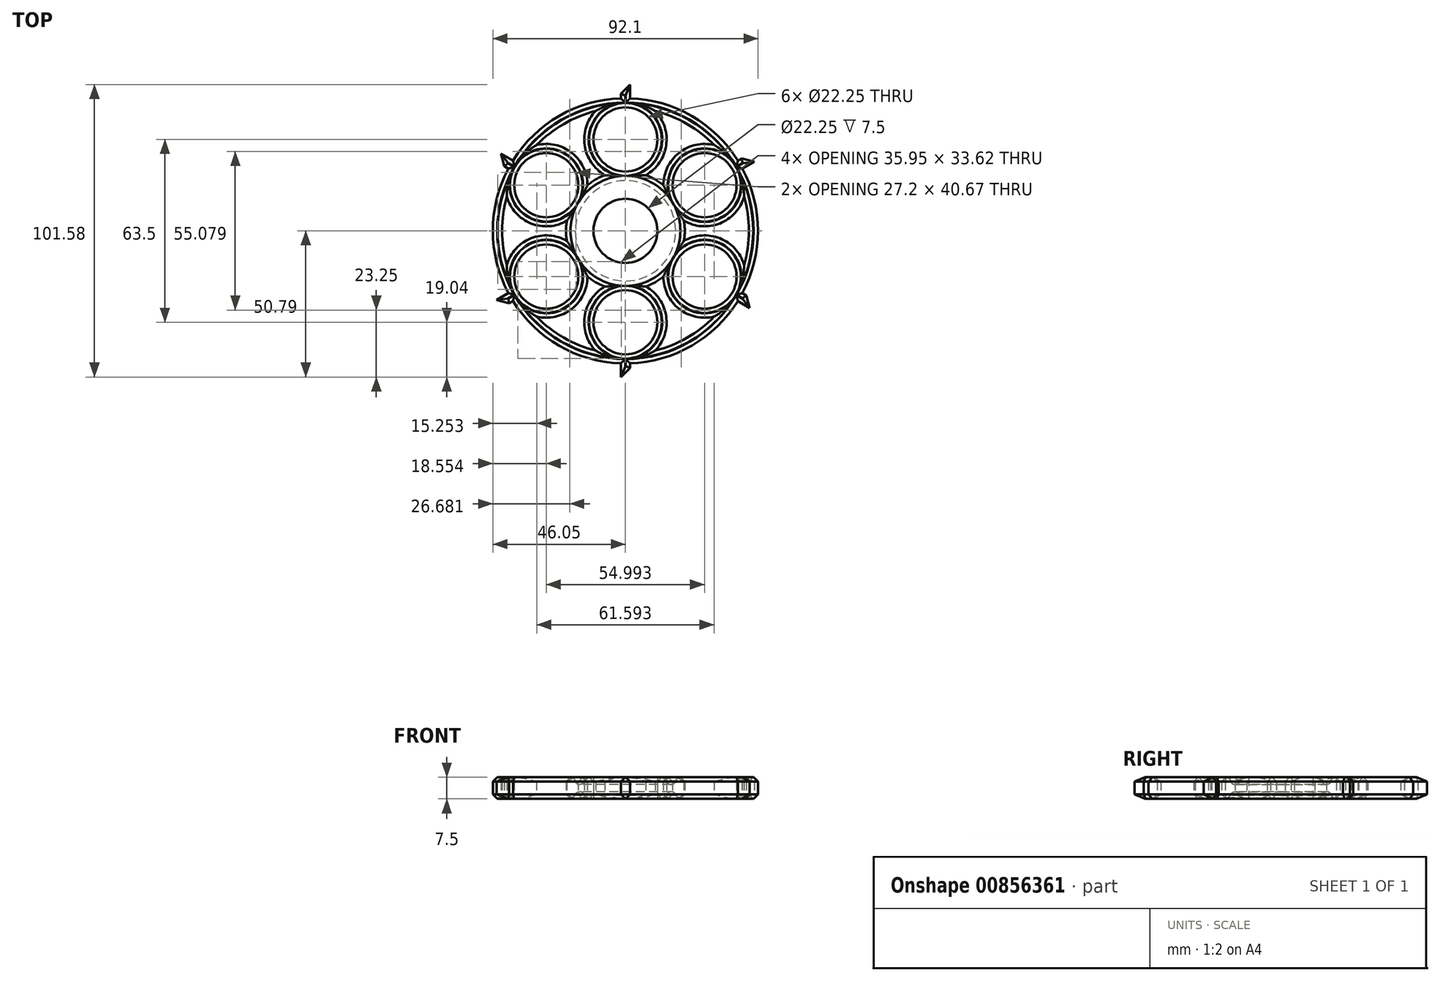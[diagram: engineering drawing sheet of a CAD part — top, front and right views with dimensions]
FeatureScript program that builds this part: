
annotation { "Feature Type Name" : "Feature", "Feature Type Description" : "" }
export const myFeature = defineFeature(function(context is Context, id is Id, definition is map)
    precondition{}
    {
        {
            var Q0;
            Q0=qCreatedBy(makeId("Top.planeOp"),FACE);
            var sketch = newSketch(context, id + "F0", { "sketchPlane" : qUnion([Q0])});
            skCircle(sketch, "E0", {"center": v(0, 0) * mm, "radius": 11.12 * mm});
            skCircle(sketch, "E1", {"center": v(0, 31.75) * mm, "radius": 11.12 * mm});
            skCircle(sketch, "E2", {"center": v(0, -31.75) * mm, "radius": 11.12 * mm});
            skCircle(sketch, "E3", {"center": v(0, 31.75) * mm, "radius": 14.3 * mm});
            skCircle(sketch, "E4", {"center": v(0, 0) * mm, "radius": 14.3 * mm});
            skCircle(sketch, "E5", {"center": v(0, -31.75) * mm, "radius": 14.3 * mm});
            skCircle(sketch, "E6", {"center": v(0, 0) * mm, "radius": 42.88 * mm});
            skCircle(sketch, "E7", {"center": v(0, 0) * mm, "radius": 46.05 * mm});
            skCircle(sketch, "E8.1.0", {"center": v(27.5, 15.87) * mm, "radius": 14.3 * mm});
            skCircle(sketch, "E8.1.1", {"center": v(27.5, 15.87) * mm, "radius": 11.12 * mm});
            skCircle(sketch, "E8.1.2", {"center": v(-27.5, -15.87) * mm, "radius": 11.12 * mm});
            skCircle(sketch, "E8.1.3", {"center": v(-27.5, -15.87) * mm, "radius": 14.3 * mm});
            skCircle(sketch, "E8.2.0", {"center": v(-27.5, 15.88) * mm, "radius": 14.3 * mm});
            skCircle(sketch, "E8.2.1", {"center": v(-27.5, 15.88) * mm, "radius": 11.12 * mm});
            skCircle(sketch, "E8.2.2", {"center": v(27.5, -15.88) * mm, "radius": 11.12 * mm});
            skCircle(sketch, "E8.2.3", {"center": v(27.5, -15.88) * mm, "radius": 14.3 * mm});
            skCircle(sketch, "E9", {"center": v(0, 0) * mm, "radius": 20.62 * mm});
            skCircle(sketch, "E10", {"center": v(0, 0) * mm, "radius": 17.45 * mm});
            skLineSegment(sketch, "E11.bottom", {"start": v(-1.59, 44.46) * mm, "end": v(1.59, 44.46) * mm});
            skLineSegment(sketch, "E11.top", {"start": v(-1.59, 50.79) * mm, "end": v(1.59, 50.79) * mm});
            skLineSegment(sketch, "E11.left", {"start": v(-1.59, 44.46) * mm, "end": v(-1.59, 50.79) * mm});
            skLineSegment(sketch, "E11.right", {"start": v(1.59, 44.46) * mm, "end": v(1.59, 50.79) * mm});
            skPoint(sketch, "E11.middle", {"position": v(0, 47.62) * mm});
            skCircle(sketch, "E12", {"center": v(0, 63.5) * mm, "radius": 11.12 * mm});
            skLineSegment(sketch, "E13", {"start": v(1.59, 50.79) * mm, "end": v(-1.59, 47.61) * mm});
            skLineSegment(sketch, "E14.1.0", {"start": v(-39.3, 20.86) * mm, "end": v(-37.71, 23.6) * mm});
            skLineSegment(sketch, "E14.1.1", {"start": v(-37.71, 23.6) * mm, "end": v(-43.19, 26.77) * mm});
            skLineSegment(sketch, "E14.1.2", {"start": v(-43.19, 26.77) * mm, "end": v(-42.03, 22.43) * mm});
            skLineSegment(sketch, "E14.1.3", {"start": v(-39.3, 20.86) * mm, "end": v(-44.78, 24.02) * mm});
            skLineSegment(sketch, "E14.2.0", {"start": v(-37.71, -23.6) * mm, "end": v(-39.3, -20.86) * mm});
            skLineSegment(sketch, "E14.2.1", {"start": v(-39.3, -20.86) * mm, "end": v(-44.78, -24.02) * mm});
            skLineSegment(sketch, "E14.2.2", {"start": v(-44.78, -24.02) * mm, "end": v(-40.44, -25.18) * mm});
            skLineSegment(sketch, "E14.2.3", {"start": v(-37.71, -23.6) * mm, "end": v(-43.19, -26.77) * mm});
            skLineSegment(sketch, "E14.3.0", {"start": v(1.59, -44.46) * mm, "end": v(-1.59, -44.46) * mm});
            skLineSegment(sketch, "E14.3.1", {"start": v(-1.59, -44.46) * mm, "end": v(-1.59, -50.79) * mm});
            skLineSegment(sketch, "E14.3.2", {"start": v(-1.59, -50.79) * mm, "end": v(1.59, -47.61) * mm});
            skLineSegment(sketch, "E14.3.3", {"start": v(1.59, -44.46) * mm, "end": v(1.59, -50.79) * mm});
            skLineSegment(sketch, "E14.4.0", {"start": v(39.3, -20.86) * mm, "end": v(37.71, -23.6) * mm});
            skLineSegment(sketch, "E14.4.1", {"start": v(37.71, -23.6) * mm, "end": v(43.19, -26.77) * mm});
            skLineSegment(sketch, "E14.4.2", {"start": v(43.19, -26.77) * mm, "end": v(42.03, -22.43) * mm});
            skLineSegment(sketch, "E14.4.3", {"start": v(39.3, -20.86) * mm, "end": v(44.78, -24.02) * mm});
            skLineSegment(sketch, "E14.5.0", {"start": v(37.71, 23.6) * mm, "end": v(39.3, 20.86) * mm});
            skLineSegment(sketch, "E14.5.1", {"start": v(39.3, 20.86) * mm, "end": v(44.78, 24.02) * mm});
            skLineSegment(sketch, "E14.5.2", {"start": v(44.78, 24.02) * mm, "end": v(40.44, 25.18) * mm});
            skLineSegment(sketch, "E14.5.3", {"start": v(37.71, 23.6) * mm, "end": v(43.19, 26.77) * mm});
            skSolve(sketch);
        }
        {
            var Q0;
            {var subQ0=sQuery(id+"F0.wireOp",EDGE,"E6");var subQ1=sQuery(id+"F0.wireOp",EDGE,"E1");var subQ2=makeQuery(id+"F0.imprint","INTERSECT",VERTEX,{"derivedFrom":[subQ1,subQ0]});Q0=makeQuery(id+"F0.imprint","IMPRINT",FACE,{"disambiguationData":[TD([[makeQuery(id+"F0.imprint","IMPRINT",EDGE,{"disambiguationData":[TD([[subQ2,1.0]])],"derivedFrom":subQ1}),-1.0]])]});}
            var Q1;
            {var subQ0=sQuery(id+"F0.wireOp",EDGE,"E6");var subQ1=sQuery(id+"F0.wireOp",EDGE,"E1");var subQ2=makeQuery(id+"F0.imprint","INTERSECT",VERTEX,{"derivedFrom":[subQ1,subQ0]});Q1=makeQuery(id+"F0.imprint","IMPRINT",FACE,{"disambiguationData":[TD([[makeQuery(id+"F0.imprint","IMPRINT",EDGE,{"disambiguationData":[TD([[subQ2,-1.0]])],"derivedFrom":subQ1}),-1.0]])]});}
            var Q2;
            {var subQ0=sQuery(id+"F0.wireOp",EDGE,"E9");var subQ1=sQuery(id+"F0.wireOp",EDGE,"E3");var subQ2=makeQuery(id+"F0.imprint","INTERSECT",VERTEX,{"disambiguationData":[OD(0.0)],"derivedFrom":[subQ1,subQ0]});Q2=makeQuery(id+"F0.imprint","IMPRINT",FACE,{"disambiguationData":[TD([[makeQuery(id+"F0.imprint","IMPRINT",EDGE,{"disambiguationData":[TD([[subQ2,-1.0]])],"derivedFrom":subQ1}),1.0]])]});}
            var Q3;
            {var subQ0=sQuery(id+"F0.wireOp",EDGE,"E8.1.0");var subQ1=makeQuery(id+"F0.imprint","INTERSECT",VERTEX,{"derivedFrom":[subQ0,sQuery(id+"F0.wireOp",EDGE,"E10")]});Q3=makeQuery(id+"F0.imprint","IMPRINT",FACE,{"disambiguationData":[TD([[makeQuery(id+"F0.imprint","IMPRINT",EDGE,{"disambiguationData":[TD([[subQ1,1.0]])],"derivedFrom":subQ0}),1.0]])]});}
            var Q4;
            {var subQ0=sQuery(id+"F0.wireOp",EDGE,"E10");var subQ1=sQuery(id+"F0.wireOp",EDGE,"E3");var subQ2=makeQuery(id+"F0.imprint","INTERSECT",VERTEX,{"derivedFrom":[subQ1,subQ0]});Q4=makeQuery(id+"F0.imprint","IMPRINT",FACE,{"disambiguationData":[TD([[makeQuery(id+"F0.imprint","IMPRINT",EDGE,{"disambiguationData":[TD([[subQ2,-1.0]])],"derivedFrom":subQ1}),-1.0]])]});}
            var Q5;
            {var subQ0=sQuery(id+"F0.wireOp",EDGE,"E10");var subQ1=sQuery(id+"F0.wireOp",EDGE,"E8.1.0");var subQ2=makeQuery(id+"F0.imprint","INTERSECT",VERTEX,{"derivedFrom":[subQ1,subQ0]});Q5=makeQuery(id+"F0.imprint","IMPRINT",FACE,{"disambiguationData":[TD([[makeQuery(id+"F0.imprint","IMPRINT",EDGE,{"disambiguationData":[TD([[subQ2,-1.0]])],"derivedFrom":subQ1}),-1.0]])]});}
            var Q6;
            {var subQ0=sQuery(id+"F0.wireOp",EDGE,"E9");var subQ1=sQuery(id+"F0.wireOp",EDGE,"E8.2.3");var subQ2=makeQuery(id+"F0.imprint","INTERSECT",VERTEX,{"disambiguationData":[OD(0.0)],"derivedFrom":[subQ1,subQ0]});Q6=makeQuery(id+"F0.imprint","IMPRINT",FACE,{"disambiguationData":[TD([[makeQuery(id+"F0.imprint","IMPRINT",EDGE,{"disambiguationData":[TD([[subQ2,-1.0]])],"derivedFrom":subQ1}),1.0]])]});}
            var Q7;
            {var subQ0=sQuery(id+"F0.wireOp",EDGE,"E10");var subQ1=sQuery(id+"F0.wireOp",EDGE,"E5");var subQ2=makeQuery(id+"F0.imprint","INTERSECT",VERTEX,{"derivedFrom":[subQ1,subQ0]});Q7=makeQuery(id+"F0.imprint","IMPRINT",FACE,{"disambiguationData":[TD([[makeQuery(id+"F0.imprint","IMPRINT",EDGE,{"disambiguationData":[TD([[subQ2,1.0]])],"derivedFrom":subQ1}),-1.0]])]});}
            var Q8;
            {var subQ0=sQuery(id+"F0.wireOp",EDGE,"E5");var subQ1=makeQuery(id+"F0.imprint","INTERSECT",VERTEX,{"derivedFrom":[subQ0,sQuery(id+"F0.wireOp",EDGE,"E10")]});Q8=makeQuery(id+"F0.imprint","IMPRINT",FACE,{"disambiguationData":[TD([[makeQuery(id+"F0.imprint","IMPRINT",EDGE,{"disambiguationData":[TD([[subQ1,1.0]])],"derivedFrom":subQ0}),1.0]])]});}
            var Q9;
            {var subQ0=sQuery(id+"F0.wireOp",EDGE,"E10");var subQ1=sQuery(id+"F0.wireOp",EDGE,"E5");var subQ2=makeQuery(id+"F0.imprint","INTERSECT",VERTEX,{"derivedFrom":[subQ1,subQ0]});Q9=makeQuery(id+"F0.imprint","IMPRINT",FACE,{"disambiguationData":[TD([[makeQuery(id+"F0.imprint","IMPRINT",EDGE,{"disambiguationData":[TD([[subQ2,-1.0]])],"derivedFrom":subQ1}),-1.0]])]});}
            var Q10;
            {var subQ0=sQuery(id+"F0.wireOp",EDGE,"E9");var subQ1=sQuery(id+"F0.wireOp",EDGE,"E8.1.3");var subQ2=makeQuery(id+"F0.imprint","INTERSECT",VERTEX,{"disambiguationData":[OD(0.0)],"derivedFrom":[subQ1,subQ0]});Q10=makeQuery(id+"F0.imprint","IMPRINT",FACE,{"disambiguationData":[TD([[makeQuery(id+"F0.imprint","IMPRINT",EDGE,{"disambiguationData":[TD([[subQ2,-1.0]])],"derivedFrom":subQ1}),1.0]])]});}
            var Q11;
            {var subQ0=sQuery(id+"F0.wireOp",EDGE,"E10");var subQ1=sQuery(id+"F0.wireOp",EDGE,"E8.1.3");var subQ2=makeQuery(id+"F0.imprint","INTERSECT",VERTEX,{"derivedFrom":[subQ1,subQ0]});Q11=makeQuery(id+"F0.imprint","IMPRINT",FACE,{"disambiguationData":[TD([[makeQuery(id+"F0.imprint","IMPRINT",EDGE,{"disambiguationData":[TD([[subQ2,-1.0]])],"derivedFrom":subQ1}),-1.0]])]});}
            var Q12;
            {var subQ0=sQuery(id+"F0.wireOp",EDGE,"E8.2.0");var subQ1=makeQuery(id+"F0.imprint","INTERSECT",VERTEX,{"derivedFrom":[subQ0,sQuery(id+"F0.wireOp",EDGE,"E10")]});Q12=makeQuery(id+"F0.imprint","IMPRINT",FACE,{"disambiguationData":[TD([[makeQuery(id+"F0.imprint","IMPRINT",EDGE,{"disambiguationData":[TD([[subQ1,1.0]])],"derivedFrom":subQ0}),1.0]])]});}
            var Q13;
            {var subQ0=sQuery(id+"F0.wireOp",EDGE,"E9");var subQ1=sQuery(id+"F0.wireOp",EDGE,"E3");var subQ2=makeQuery(id+"F0.imprint","INTERSECT",VERTEX,{"disambiguationData":[OD(0.0)],"derivedFrom":[subQ1,subQ0]});Q13=makeQuery(id+"F0.imprint","IMPRINT",FACE,{"disambiguationData":[TD([[makeQuery(id+"F0.imprint","IMPRINT",EDGE,{"disambiguationData":[TD([[subQ2,-1.0]])],"derivedFrom":subQ1}),-1.0]])]});}
            var Q14;
            {var subQ0=sQuery(id+"F0.wireOp",EDGE,"E8.2.0");var subQ1=sQuery(id+"F0.wireOp",EDGE,"E6");var subQ2=makeQuery(id+"F0.imprint","INTERSECT",VERTEX,{"disambiguationData":[OD(0.0)],"derivedFrom":[subQ1,subQ0]});Q14=makeQuery(id+"F0.imprint","IMPRINT",FACE,{"disambiguationData":[TD([[makeQuery(id+"F0.imprint","IMPRINT",EDGE,{"disambiguationData":[TD([[subQ2,-1.0]])],"derivedFrom":subQ1}),1.0]])]});}
            var Q15;
            {var subQ0=sQuery(id+"F0.wireOp",EDGE,"E8.2.1");var subQ1=sQuery(id+"F0.wireOp",EDGE,"E6");var subQ2=makeQuery(id+"F0.imprint","INTERSECT",VERTEX,{"derivedFrom":[subQ1,subQ0]});Q15=makeQuery(id+"F0.imprint","IMPRINT",FACE,{"disambiguationData":[TD([[makeQuery(id+"F0.imprint","IMPRINT",EDGE,{"disambiguationData":[TD([[subQ2,-1.0]])],"derivedFrom":subQ1}),1.0]])]});}
            var Q16;
            {var subQ0=sQuery(id+"F0.wireOp",EDGE,"E8.1.1");var subQ1=sQuery(id+"F0.wireOp",EDGE,"E6");var subQ2=makeQuery(id+"F0.imprint","INTERSECT",VERTEX,{"derivedFrom":[subQ1,subQ0]});Q16=makeQuery(id+"F0.imprint","IMPRINT",FACE,{"disambiguationData":[TD([[makeQuery(id+"F0.imprint","IMPRINT",EDGE,{"disambiguationData":[TD([[subQ2,-1.0]])],"derivedFrom":subQ1}),1.0]])]});}
            var Q17;
            {var subQ0=sQuery(id+"F0.wireOp",EDGE,"E8.1.1");var subQ1=sQuery(id+"F0.wireOp",EDGE,"E6");var subQ2=makeQuery(id+"F0.imprint","INTERSECT",VERTEX,{"derivedFrom":[subQ1,subQ0]});Q17=makeQuery(id+"F0.imprint","IMPRINT",FACE,{"disambiguationData":[TD([[makeQuery(id+"F0.imprint","IMPRINT",EDGE,{"disambiguationData":[TD([[subQ2,1.0]])],"derivedFrom":subQ1}),1.0]])]});}
            var Q18;
            {var subQ0=sQuery(id+"F0.wireOp",EDGE,"E8.2.2");var subQ1=sQuery(id+"F0.wireOp",EDGE,"E6");var subQ2=makeQuery(id+"F0.imprint","INTERSECT",VERTEX,{"derivedFrom":[subQ1,subQ0]});Q18=makeQuery(id+"F0.imprint","IMPRINT",FACE,{"disambiguationData":[TD([[makeQuery(id+"F0.imprint","IMPRINT",EDGE,{"disambiguationData":[TD([[subQ2,-1.0]])],"derivedFrom":subQ1}),1.0]])]});}
            var Q19;
            {var subQ0=sQuery(id+"F0.wireOp",EDGE,"E8.2.3");var subQ1=sQuery(id+"F0.wireOp",EDGE,"E6");var subQ2=makeQuery(id+"F0.imprint","INTERSECT",VERTEX,{"disambiguationData":[OD(0.0)],"derivedFrom":[subQ1,subQ0]});Q19=makeQuery(id+"F0.imprint","IMPRINT",FACE,{"disambiguationData":[TD([[makeQuery(id+"F0.imprint","IMPRINT",EDGE,{"disambiguationData":[TD([[subQ2,-1.0]])],"derivedFrom":subQ1}),1.0]])]});}
            var Q20;
            {var subQ0=sQuery(id+"F0.wireOp",EDGE,"E6");var subQ1=sQuery(id+"F0.wireOp",EDGE,"E2");var subQ2=makeQuery(id+"F0.imprint","INTERSECT",VERTEX,{"derivedFrom":[subQ1,subQ0]});Q20=makeQuery(id+"F0.imprint","IMPRINT",FACE,{"disambiguationData":[TD([[makeQuery(id+"F0.imprint","IMPRINT",EDGE,{"disambiguationData":[TD([[subQ2,1.0]])],"derivedFrom":subQ1}),-1.0]])]});}
            var Q21;
            {var subQ0=sQuery(id+"F0.wireOp",EDGE,"E6");var subQ1=sQuery(id+"F0.wireOp",EDGE,"E2");var subQ2=makeQuery(id+"F0.imprint","INTERSECT",VERTEX,{"derivedFrom":[subQ1,subQ0]});Q21=makeQuery(id+"F0.imprint","IMPRINT",FACE,{"disambiguationData":[TD([[makeQuery(id+"F0.imprint","IMPRINT",EDGE,{"disambiguationData":[TD([[subQ2,-1.0]])],"derivedFrom":subQ1}),-1.0]])]});}
            var Q22;
            {var subQ0=sQuery(id+"F0.wireOp",EDGE,"E8.1.2");var subQ1=sQuery(id+"F0.wireOp",EDGE,"E6");var subQ2=makeQuery(id+"F0.imprint","INTERSECT",VERTEX,{"derivedFrom":[subQ1,subQ0]});Q22=makeQuery(id+"F0.imprint","IMPRINT",FACE,{"disambiguationData":[TD([[makeQuery(id+"F0.imprint","IMPRINT",EDGE,{"disambiguationData":[TD([[subQ2,-1.0]])],"derivedFrom":subQ1}),1.0]])]});}
            var Q23;
            {var subQ0=sQuery(id+"F0.wireOp",EDGE,"E8.1.3");var subQ1=sQuery(id+"F0.wireOp",EDGE,"E6");var subQ2=makeQuery(id+"F0.imprint","INTERSECT",VERTEX,{"disambiguationData":[OD(0.0)],"derivedFrom":[subQ1,subQ0]});Q23=makeQuery(id+"F0.imprint","IMPRINT",FACE,{"disambiguationData":[TD([[makeQuery(id+"F0.imprint","IMPRINT",EDGE,{"disambiguationData":[TD([[subQ2,-1.0]])],"derivedFrom":subQ1}),1.0]])]});}
            var Q24;
            Q24=makeQuery(id+"F0.imprint","IMPRINT",FACE,{"disambiguationData":[TD([[makeQuery(id+"F0.imprint","IMPRINT",EDGE,{"derivedFrom":sQuery(id+"F0.wireOp",EDGE,"E0")}),-1.0]])]});
            var Q25;
            Q25=makeQuery(id+"F0.imprint","IMPRINT",FACE,{"disambiguationData":[TD([[makeQuery(id+"F0.imprint","IMPRINT",EDGE,{"derivedFrom":sQuery(id+"F0.wireOp",EDGE,"E4")}),-1.0]])]});
            var Q26;
            {var subQ5=sQuery(id+"F0.wireOp",EDGE,"E11.left");var subQ8=sQuery(id+"F0.wireOp",EDGE,"E3");var subQ9=makeQuery(id+"F0.imprint","INTERSECT",VERTEX,{"derivedFrom":[subQ8,subQ5]});Q26=makeQuery(id+"F0.imprint","IMPRINT",FACE,{"disambiguationData":[TD([[makeQuery(id+"F0.imprint","IMPRINT",EDGE,{"disambiguationData":[TD([[subQ9,-1.0]])],"derivedFrom":subQ8}),-1.0]])]});}
            var Q27;
            {var subQ9=sQuery(id+"F0.wireOp",EDGE,"E14.1.0");Q27=makeQuery(id+"F0.imprint","IMPRINT",FACE,{"disambiguationData":[TD([[makeQuery(id+"F0.imprint","IMPRINT",EDGE,{"derivedFrom":subQ9}),-1.0]])]});}
            var Q28;
            {var subQ7=sQuery(id+"F0.wireOp",EDGE,"E11.bottom");Q28=makeQuery(id+"F0.imprint","IMPRINT",FACE,{"disambiguationData":[TD([[makeQuery(id+"F0.imprint","IMPRINT",EDGE,{"derivedFrom":subQ7}),-1.0]])]});}
            var Q29;
            {var subQ3=sQuery(id+"F0.wireOp",EDGE,"E11.right");var subQ9=sQuery(id+"F0.wireOp",EDGE,"E3");var subQ11=makeQuery(id+"F0.imprint","INTERSECT",VERTEX,{"derivedFrom":[subQ9,subQ3]});Q29=makeQuery(id+"F0.imprint","IMPRINT",FACE,{"disambiguationData":[TD([[makeQuery(id+"F0.imprint","IMPRINT",EDGE,{"disambiguationData":[TD([[subQ11,1.0]])],"derivedFrom":subQ9}),-1.0]])]});}
            var Q30;
            {var subQ0=sQuery(id+"F0.wireOp",EDGE,"E8.2.0");var subQ1=sQuery(id+"F0.wireOp",EDGE,"E6");var subQ2=makeQuery(id+"F0.imprint","INTERSECT",VERTEX,{"disambiguationData":[OD(1.0)],"derivedFrom":[subQ1,subQ0]});Q30=makeQuery(id+"F0.imprint","IMPRINT",FACE,{"disambiguationData":[TD([[makeQuery(id+"F0.imprint","IMPRINT",EDGE,{"disambiguationData":[TD([[subQ2,-1.0]])],"derivedFrom":subQ1}),-1.0]])]});}
            var Q31;
            {var subQ9=sQuery(id+"F0.wireOp",EDGE,"E14.5.0");Q31=makeQuery(id+"F0.imprint","IMPRINT",FACE,{"disambiguationData":[TD([[makeQuery(id+"F0.imprint","IMPRINT",EDGE,{"derivedFrom":subQ9}),-1.0]])]});}
            var Q32;
            {var subQ1=sQuery(id+"F0.wireOp",EDGE,"E6");var subQ5=sQuery(id+"F0.wireOp",EDGE,"E8.1.0");var subQ6=makeQuery(id+"F0.imprint","INTERSECT",VERTEX,{"disambiguationData":[OD(0.0)],"derivedFrom":[subQ1,subQ5]});Q32=makeQuery(id+"F0.imprint","IMPRINT",FACE,{"disambiguationData":[TD([[makeQuery(id+"F0.imprint","IMPRINT",EDGE,{"disambiguationData":[TD([[subQ6,1.0]])],"derivedFrom":subQ1}),-1.0]])]});}
            var Q33;
            {var subQ9=sQuery(id+"F0.wireOp",EDGE,"E14.4.0");Q33=makeQuery(id+"F0.imprint","IMPRINT",FACE,{"disambiguationData":[TD([[makeQuery(id+"F0.imprint","IMPRINT",EDGE,{"derivedFrom":subQ9}),-1.0]])]});}
            var Q34;
            {var subQ0=sQuery(id+"F0.wireOp",EDGE,"E14.3.3");var subQ6=sQuery(id+"F0.wireOp",EDGE,"E5");var subQ11=makeQuery(id+"F0.imprint","INTERSECT",VERTEX,{"derivedFrom":[subQ6,subQ0]});Q34=makeQuery(id+"F0.imprint","IMPRINT",FACE,{"disambiguationData":[TD([[makeQuery(id+"F0.imprint","IMPRINT",EDGE,{"disambiguationData":[TD([[subQ11,-1.0]])],"derivedFrom":subQ6}),-1.0]])]});}
            var Q35;
            {var subQ9=sQuery(id+"F0.wireOp",EDGE,"E14.3.0");Q35=makeQuery(id+"F0.imprint","IMPRINT",FACE,{"disambiguationData":[TD([[makeQuery(id+"F0.imprint","IMPRINT",EDGE,{"derivedFrom":subQ9}),-1.0]])]});}
            var Q36;
            {var subQ6=sQuery(id+"F0.wireOp",EDGE,"E6");var subQ9=sQuery(id+"F0.wireOp",EDGE,"E5");var subQ10=makeQuery(id+"F0.imprint","INTERSECT",VERTEX,{"disambiguationData":[OD(0.0)],"derivedFrom":[subQ9,subQ6]});Q36=makeQuery(id+"F0.imprint","IMPRINT",FACE,{"disambiguationData":[TD([[makeQuery(id+"F0.imprint","IMPRINT",EDGE,{"disambiguationData":[TD([[subQ10,-1.0]])],"derivedFrom":subQ9}),-1.0]])]});}
            var Q37;
            {var subQ9=sQuery(id+"F0.wireOp",EDGE,"E14.2.0");Q37=makeQuery(id+"F0.imprint","IMPRINT",FACE,{"disambiguationData":[TD([[makeQuery(id+"F0.imprint","IMPRINT",EDGE,{"derivedFrom":subQ9}),-1.0]])]});}
            var Q38;
            {var subQ1=sQuery(id+"F0.wireOp",EDGE,"E11.bottom");Q38=makeQuery(id+"F0.imprint","IMPRINT",FACE,{"disambiguationData":[TD([[makeQuery(id+"F0.imprint","IMPRINT",EDGE,{"derivedFrom":subQ1}),1.0]])]});}
            var Q39;
            {var subQ0=sQuery(id+"F0.wireOp",EDGE,"E13");Q39=makeQuery(id+"F0.imprint","IMPRINT",FACE,{"disambiguationData":[TD([[makeQuery(id+"F0.imprint","IMPRINT",EDGE,{"derivedFrom":subQ0}),1.0]])]});}
            var Q40;
            {var subQ0=sQuery(id+"F0.wireOp",EDGE,"E11.right");var subQ1=sQuery(id+"F0.wireOp",EDGE,"E3");var subQ2=makeQuery(id+"F0.imprint","INTERSECT",VERTEX,{"derivedFrom":[subQ1,subQ0]});Q40=makeQuery(id+"F0.imprint","IMPRINT",FACE,{"disambiguationData":[TD([[makeQuery(id+"F0.imprint","IMPRINT",EDGE,{"disambiguationData":[TD([[subQ2,-1.0]])],"derivedFrom":subQ1}),-1.0]])]});}
            var Q41;
            {var subQ0=sQuery(id+"F0.wireOp",EDGE,"E7");var subQ1=sQuery(id+"F0.wireOp",EDGE,"E3");var subQ2=makeQuery(id+"F0.imprint","INTERSECT",VERTEX,{"derivedFrom":[subQ1,subQ0]});Q41=makeQuery(id+"F0.imprint","IMPRINT",FACE,{"disambiguationData":[TD([[makeQuery(id+"F0.imprint","IMPRINT",EDGE,{"disambiguationData":[TD([[subQ2,-1.0]])],"derivedFrom":subQ1}),-1.0]])]});}
            var Q42;
            {var subQ0=sQuery(id+"F0.wireOp",EDGE,"E14.1.1");var subQ1=sQuery(id+"F0.wireOp",EDGE,"E7");var subQ2=makeQuery(id+"F0.imprint","INTERSECT",VERTEX,{"derivedFrom":[subQ1,subQ0]});Q42=makeQuery(id+"F0.imprint","IMPRINT",FACE,{"disambiguationData":[TD([[makeQuery(id+"F0.imprint","IMPRINT",EDGE,{"disambiguationData":[TD([[subQ2,-1.0]])],"derivedFrom":subQ1}),1.0]])]});}
            var Q43;
            {var subQ1=sQuery(id+"F0.wireOp",EDGE,"E14.1.0");Q43=makeQuery(id+"F0.imprint","IMPRINT",FACE,{"disambiguationData":[TD([[makeQuery(id+"F0.imprint","IMPRINT",EDGE,{"derivedFrom":subQ1}),1.0]])]});}
            var Q44;
            {var subQ0=sQuery(id+"F0.wireOp",EDGE,"E14.1.2");Q44=makeQuery(id+"F0.imprint","IMPRINT",FACE,{"disambiguationData":[TD([[makeQuery(id+"F0.imprint","IMPRINT",EDGE,{"derivedFrom":subQ0}),1.0]])]});}
            var Q45;
            {var subQ0=sQuery(id+"F0.wireOp",EDGE,"E14.1.3");var subQ1=sQuery(id+"F0.wireOp",EDGE,"E7");var subQ2=makeQuery(id+"F0.imprint","INTERSECT",VERTEX,{"derivedFrom":[subQ1,subQ0]});Q45=makeQuery(id+"F0.imprint","IMPRINT",FACE,{"disambiguationData":[TD([[makeQuery(id+"F0.imprint","IMPRINT",EDGE,{"disambiguationData":[TD([[subQ2,1.0]])],"derivedFrom":subQ1}),1.0]])]});}
            var Q46;
            {var subQ0=sQuery(id+"F0.wireOp",EDGE,"E14.2.1");var subQ1=sQuery(id+"F0.wireOp",EDGE,"E7");var subQ2=makeQuery(id+"F0.imprint","INTERSECT",VERTEX,{"derivedFrom":[subQ1,subQ0]});Q46=makeQuery(id+"F0.imprint","IMPRINT",FACE,{"disambiguationData":[TD([[makeQuery(id+"F0.imprint","IMPRINT",EDGE,{"disambiguationData":[TD([[subQ2,-1.0]])],"derivedFrom":subQ1}),1.0]])]});}
            var Q47;
            {var subQ1=sQuery(id+"F0.wireOp",EDGE,"E14.2.0");Q47=makeQuery(id+"F0.imprint","IMPRINT",FACE,{"disambiguationData":[TD([[makeQuery(id+"F0.imprint","IMPRINT",EDGE,{"derivedFrom":subQ1}),1.0]])]});}
            var Q48;
            {var subQ0=sQuery(id+"F0.wireOp",EDGE,"E14.2.3");var subQ1=sQuery(id+"F0.wireOp",EDGE,"E7");var subQ2=makeQuery(id+"F0.imprint","INTERSECT",VERTEX,{"derivedFrom":[subQ1,subQ0]});Q48=makeQuery(id+"F0.imprint","IMPRINT",FACE,{"disambiguationData":[TD([[makeQuery(id+"F0.imprint","IMPRINT",EDGE,{"disambiguationData":[TD([[subQ2,1.0]])],"derivedFrom":subQ1}),1.0]])]});}
            var Q49;
            {var subQ0=sQuery(id+"F0.wireOp",EDGE,"E14.2.2");Q49=makeQuery(id+"F0.imprint","IMPRINT",FACE,{"disambiguationData":[TD([[makeQuery(id+"F0.imprint","IMPRINT",EDGE,{"derivedFrom":subQ0}),1.0]])]});}
            var Q50;
            {var subQ1=sQuery(id+"F0.wireOp",EDGE,"E14.3.0");Q50=makeQuery(id+"F0.imprint","IMPRINT",FACE,{"disambiguationData":[TD([[makeQuery(id+"F0.imprint","IMPRINT",EDGE,{"derivedFrom":subQ1}),1.0]])]});}
            var Q51;
            {var subQ0=sQuery(id+"F0.wireOp",EDGE,"E14.3.1");var subQ1=sQuery(id+"F0.wireOp",EDGE,"E5");var subQ2=makeQuery(id+"F0.imprint","INTERSECT",VERTEX,{"derivedFrom":[subQ1,subQ0]});Q51=makeQuery(id+"F0.imprint","IMPRINT",FACE,{"disambiguationData":[TD([[makeQuery(id+"F0.imprint","IMPRINT",EDGE,{"disambiguationData":[TD([[subQ2,-1.0]])],"derivedFrom":subQ1}),-1.0]])]});}
            var Q52;
            {var subQ0=sQuery(id+"F0.wireOp",EDGE,"E14.3.2");Q52=makeQuery(id+"F0.imprint","IMPRINT",FACE,{"disambiguationData":[TD([[makeQuery(id+"F0.imprint","IMPRINT",EDGE,{"derivedFrom":subQ0}),1.0]])]});}
            var Q53;
            {var subQ0=sQuery(id+"F0.wireOp",EDGE,"E7");var subQ1=sQuery(id+"F0.wireOp",EDGE,"E5");var subQ2=makeQuery(id+"F0.imprint","INTERSECT",VERTEX,{"derivedFrom":[subQ1,subQ0]});Q53=makeQuery(id+"F0.imprint","IMPRINT",FACE,{"disambiguationData":[TD([[makeQuery(id+"F0.imprint","IMPRINT",EDGE,{"disambiguationData":[TD([[subQ2,-1.0]])],"derivedFrom":subQ1}),-1.0]])]});}
            var Q54;
            {var subQ1=sQuery(id+"F0.wireOp",EDGE,"E14.4.0");Q54=makeQuery(id+"F0.imprint","IMPRINT",FACE,{"disambiguationData":[TD([[makeQuery(id+"F0.imprint","IMPRINT",EDGE,{"derivedFrom":subQ1}),1.0]])]});}
            var Q55;
            {var subQ0=sQuery(id+"F0.wireOp",EDGE,"E14.4.3");var subQ1=sQuery(id+"F0.wireOp",EDGE,"E7");var subQ2=makeQuery(id+"F0.imprint","INTERSECT",VERTEX,{"derivedFrom":[subQ1,subQ0]});Q55=makeQuery(id+"F0.imprint","IMPRINT",FACE,{"disambiguationData":[TD([[makeQuery(id+"F0.imprint","IMPRINT",EDGE,{"disambiguationData":[TD([[subQ2,1.0]])],"derivedFrom":subQ1}),1.0]])]});}
            var Q56;
            {var subQ0=sQuery(id+"F0.wireOp",EDGE,"E14.4.2");Q56=makeQuery(id+"F0.imprint","IMPRINT",FACE,{"disambiguationData":[TD([[makeQuery(id+"F0.imprint","IMPRINT",EDGE,{"derivedFrom":subQ0}),1.0]])]});}
            var Q57;
            {var subQ0=sQuery(id+"F0.wireOp",EDGE,"E14.4.1");var subQ1=sQuery(id+"F0.wireOp",EDGE,"E7");var subQ2=makeQuery(id+"F0.imprint","INTERSECT",VERTEX,{"derivedFrom":[subQ1,subQ0]});Q57=makeQuery(id+"F0.imprint","IMPRINT",FACE,{"disambiguationData":[TD([[makeQuery(id+"F0.imprint","IMPRINT",EDGE,{"disambiguationData":[TD([[subQ2,-1.0]])],"derivedFrom":subQ1}),1.0]])]});}
            var Q58;
            {var subQ0=sQuery(id+"F0.wireOp",EDGE,"E14.5.3");var subQ1=sQuery(id+"F0.wireOp",EDGE,"E7");var subQ2=makeQuery(id+"F0.imprint","INTERSECT",VERTEX,{"derivedFrom":[subQ1,subQ0]});Q58=makeQuery(id+"F0.imprint","IMPRINT",FACE,{"disambiguationData":[TD([[makeQuery(id+"F0.imprint","IMPRINT",EDGE,{"disambiguationData":[TD([[subQ2,1.0]])],"derivedFrom":subQ1}),1.0]])]});}
            var Q59;
            {var subQ0=sQuery(id+"F0.wireOp",EDGE,"E14.5.1");var subQ1=sQuery(id+"F0.wireOp",EDGE,"E7");var subQ2=makeQuery(id+"F0.imprint","INTERSECT",VERTEX,{"derivedFrom":[subQ1,subQ0]});Q59=makeQuery(id+"F0.imprint","IMPRINT",FACE,{"disambiguationData":[TD([[makeQuery(id+"F0.imprint","IMPRINT",EDGE,{"disambiguationData":[TD([[subQ2,-1.0]])],"derivedFrom":subQ1}),1.0]])]});}
            var Q60;
            {var subQ1=sQuery(id+"F0.wireOp",EDGE,"E14.5.0");Q60=makeQuery(id+"F0.imprint","IMPRINT",FACE,{"disambiguationData":[TD([[makeQuery(id+"F0.imprint","IMPRINT",EDGE,{"derivedFrom":subQ1}),1.0]])]});}
            var Q61;
            {var subQ0=sQuery(id+"F0.wireOp",EDGE,"E14.5.2");Q61=makeQuery(id+"F0.imprint","IMPRINT",FACE,{"disambiguationData":[TD([[makeQuery(id+"F0.imprint","IMPRINT",EDGE,{"derivedFrom":subQ0}),1.0]])]});}
            extrude(context, id + "F1", {"entities" : qUnion([Q0, Q1, Q2, Q3, Q4, Q5, Q6, Q7, Q8, Q9, Q10, Q11, Q12, Q13, Q14, Q15, Q16, Q17, Q18, Q19, Q20, Q21, Q22, Q23, Q24, Q25, Q26, Q27, Q28, Q29, Q30, Q31, Q32, Q33, Q34, Q35, Q36, Q37, Q38, Q39, Q40, Q41, Q42, Q43, Q44, Q45, Q46, Q47, Q48, Q49, Q50, Q51, Q52, Q53, Q54, Q55, Q56, Q57, Q58, Q59, Q60, Q61]), "depth" : 7.5 * mm, "offsetDistance" : 25 * mm});
        }
        {
            var Q0;
            Q0=makeQuery(id+"F0.imprint","IMPRINT",FACE,{"disambiguationData":[TD([[makeQuery(id+"F0.imprint","IMPRINT",EDGE,{"derivedFrom":sQuery(id+"F0.wireOp",EDGE,"E4")}),-1.0]])]});
            extrude(context, id + "F2", {"entities" : qUnion([Q0]), "operationType" : NewBodyOperationType.REMOVE, "depth" : 7.5 / 3 * mm, "offsetDistance" : 25 * mm});
        }
        {
            var Q0;
            Q0=makeQuery(id+"F0.imprint","IMPRINT",FACE,{"disambiguationData":[TD([[makeQuery(id+"F0.imprint","IMPRINT",EDGE,{"derivedFrom":sQuery(id+"F0.wireOp",EDGE,"E4")}),-1.0]])]});
            extrude(context, id + "F3", {"entities" : qUnion([Q0]), "operationType" : NewBodyOperationType.REMOVE, "depth" : 25 * mm, "offsetDistance" : 25 * mm, "hasSecondDirection" : true, "secondDirectionOppositeDirection" : false, "secondDirectionDepth" : (7.5 / 3) * 2 * mm});
        }
        {
            var Q0;
            Q0=makeQuery(id+"F3.boolean.opBoolean","COPY",EDGE,{"derivedFrom":makeQuery(id+"F3.opExtrude","CAP_EDGE",EDGE,{"disambiguationData":[OSD([sQuery(id+"F0.wireOp",EDGE,"E10")])],"isStart":true})});
            var Q1;
            Q1=makeQuery(id+"F3.boolean.opBoolean","COPY",EDGE,{"derivedFrom":makeQuery(id+"F3.opExtrude","CAP_EDGE",EDGE,{"disambiguationData":[OSD([sQuery(id+"F0.wireOp",EDGE,"E4")])],"isStart":true})});
            var Q2;
            Q2=makeQuery(id+"F2.boolean.opBoolean","COPY",EDGE,{"derivedFrom":makeQuery(id+"F2.opExtrude","CAP_EDGE",EDGE,{"disambiguationData":[OSD([sQuery(id+"F0.wireOp",EDGE,"E4")])],"isStart":false})});
            var Q3;
            Q3=makeQuery(id+"F2.boolean.opBoolean","COPY",FACE,{"derivedFrom":makeQuery(id+"F2.opExtrude","CAP_FACE",FACE,{"disambiguationData":[OSD([sQuery(id+"F0.wireOp",EDGE,"E4"),sQuery(id+"F0.wireOp",EDGE,"E10")])],"isStart":false})});
            fillet(context, id + "F4", {"entities" : qUnion([Q0, Q1, Q2, Q3]), "radius" : 1.52 * mm, "tangentPropagation" : true, "allowEdgeOverflow" : false});
        }
        {
            var Q0;
            Q0=makeQuery(id+"F3.boolean.opBoolean","INTERSECT",EDGE,{"derivedFrom":[makeQuery(id+"F1.opExtrude","CAP_FACE",FACE,{"disambiguationData":[OSD([sQuery(id+"F0.wireOp",EDGE,"E0"),sQuery(id+"F0.wireOp",EDGE,"E1"),sQuery(id+"F0.wireOp",EDGE,"E2"),sQuery(id+"F0.wireOp",EDGE,"E7"),sQuery(id+"F0.wireOp",EDGE,"E8.1.1"),sQuery(id+"F0.wireOp",EDGE,"E8.1.2"),sQuery(id+"F0.wireOp",EDGE,"E8.2.1"),sQuery(id+"F0.wireOp",EDGE,"E8.2.2")])],"isStart":false}),makeQuery(id+"F3.opExtrude","SWEPT_FACE",FACE,{"disambiguationData":[OSD([sQuery(id+"F0.wireOp",EDGE,"E10")])]})]});
            var Q1;
            Q1=makeQuery(id+"F3.boolean.opBoolean","INTERSECT",EDGE,{"derivedFrom":[makeQuery(id+"F1.opExtrude","CAP_FACE",FACE,{"disambiguationData":[OSD([sQuery(id+"F0.wireOp",EDGE,"E0"),sQuery(id+"F0.wireOp",EDGE,"E1"),sQuery(id+"F0.wireOp",EDGE,"E2"),sQuery(id+"F0.wireOp",EDGE,"E7"),sQuery(id+"F0.wireOp",EDGE,"E8.1.1"),sQuery(id+"F0.wireOp",EDGE,"E8.1.2"),sQuery(id+"F0.wireOp",EDGE,"E8.2.1"),sQuery(id+"F0.wireOp",EDGE,"E8.2.2")])],"isStart":false}),makeQuery(id+"F3.opExtrude","SWEPT_FACE",FACE,{"disambiguationData":[OSD([sQuery(id+"F0.wireOp",EDGE,"E4")])]})]});
            var Q2;
            Q2=makeQuery(id+"F2.boolean.opBoolean","COPY",EDGE,{"derivedFrom":makeQuery(id+"F2.opExtrude","CAP_EDGE",EDGE,{"disambiguationData":[OSD([sQuery(id+"F0.wireOp",EDGE,"E4")])],"isStart":true})});
            var Q3;
            Q3=makeQuery(id+"F2.boolean.opBoolean","COPY",EDGE,{"derivedFrom":makeQuery(id+"F2.opExtrude","CAP_EDGE",EDGE,{"disambiguationData":[OSD([sQuery(id+"F0.wireOp",EDGE,"E10")])],"isStart":true})});
            fillet(context, id + "F5", {"entities" : qUnion([Q0, Q1, Q2, Q3]), "radius" : 1.59 * mm, "tangentPropagation" : true, "allowEdgeOverflow" : false});
        }
        {
            var Q0;
            {var subQ0=sQuery(id+"F0.wireOp",EDGE,"E14.3.1");var subQ1=sQuery(id+"F0.wireOp",EDGE,"E14.2.3");var subQ2=sQuery(id+"F0.wireOp",EDGE,"E14.2.2");var subQ3=sQuery(id+"F0.wireOp",EDGE,"E14.2.1");var subQ4=sQuery(id+"F0.wireOp",EDGE,"E14.1.3");var subQ5=sQuery(id+"F0.wireOp",EDGE,"E14.1.2");var subQ6=sQuery(id+"F0.wireOp",EDGE,"E14.1.1");var subQ7=sQuery(id+"F0.wireOp",EDGE,"E13");var subQ8=sQuery(id+"F0.wireOp",EDGE,"E11.right");var subQ9=sQuery(id+"F0.wireOp",EDGE,"E11.left");var subQ10=sQuery(id+"F0.wireOp",EDGE,"E9");var subQ11=sQuery(id+"F0.wireOp",EDGE,"E8.1.0");var subQ13=sQuery(id+"F0.wireOp",EDGE,"E8.2.3");var subQ15=sQuery(id+"F0.wireOp",EDGE,"E5");var subQ19=sQuery(id+"F0.wireOp",EDGE,"E8.1.3");var subQ22=sQuery(id+"F0.wireOp",EDGE,"E8.2.0");var subQ24=sQuery(id+"F0.wireOp",EDGE,"E3");var subQ29=sQuery(id+"F0.wireOp",EDGE,"E6");var subQ32=sQuery(id+"F0.wireOp",EDGE,"E8.2.2");var subQ33=sQuery(id+"F0.wireOp",EDGE,"E8.2.1");var subQ43=sQuery(id+"F0.wireOp",EDGE,"E1");var subQ44=sQuery(id+"F0.wireOp",EDGE,"E2");var subQ46=sQuery(id+"F0.wireOp",EDGE,"E14.5.3");var subQ47=sQuery(id+"F0.wireOp",EDGE,"E7");var subQ48=sQuery(id+"F0.wireOp",EDGE,"E14.3.3");var subQ49=sQuery(id+"F0.wireOp",EDGE,"E14.4.1");var subQ50=sQuery(id+"F0.wireOp",EDGE,"E14.5.1");var subQ51=sQuery(id+"F0.wireOp",EDGE,"E14.4.3");var subQ52=sQuery(id+"F0.wireOp",EDGE,"E8.1.1");var subQ53=sQuery(id+"F0.wireOp",EDGE,"E8.1.2");var subQ54=sQuery(id+"F0.wireOp",EDGE,"E14.3.2");var subQ55=sQuery(id+"F0.wireOp",EDGE,"E14.4.2");var subQ56=sQuery(id+"F0.wireOp",EDGE,"E14.5.2");Q0=makeQuery(id+"F3.boolean.opBoolean","SPLIT",FACE,{"disambiguationData":[TD([makeQuery(id+"F1.opExtrude","SWEPT_FACE",FACE,{"disambiguationData":[OSD([subQ43])]})])],"derivedFrom":makeQuery(id+"F1.opExtrude","CAP_FACE",FACE,{"disambiguationData":[OSD([sQuery(id+"F0.wireOp",EDGE,"E0"),subQ43,subQ44,subQ24,subQ15,subQ29,subQ47,subQ11,subQ52,subQ53,subQ19,subQ22,subQ33,subQ32,subQ13,subQ10,subQ9,subQ8,subQ7,subQ6,subQ5,subQ4,subQ3,subQ2,subQ1,subQ0,subQ54,subQ48,subQ49,subQ55,subQ51,subQ50,subQ56,subQ46])],"isStart":false})});}
            var Q1;
            {var subQ0=sQuery(id+"F0.wireOp",EDGE,"E14.3.1");var subQ1=sQuery(id+"F0.wireOp",EDGE,"E14.2.3");var subQ2=sQuery(id+"F0.wireOp",EDGE,"E14.2.2");var subQ3=sQuery(id+"F0.wireOp",EDGE,"E14.2.1");var subQ4=sQuery(id+"F0.wireOp",EDGE,"E14.1.3");var subQ5=sQuery(id+"F0.wireOp",EDGE,"E14.1.2");var subQ6=sQuery(id+"F0.wireOp",EDGE,"E14.1.1");var subQ7=sQuery(id+"F0.wireOp",EDGE,"E13");var subQ8=sQuery(id+"F0.wireOp",EDGE,"E11.right");var subQ9=sQuery(id+"F0.wireOp",EDGE,"E11.left");var subQ10=sQuery(id+"F0.wireOp",EDGE,"E9");var subQ11=sQuery(id+"F0.wireOp",EDGE,"E8.1.0");var subQ13=sQuery(id+"F0.wireOp",EDGE,"E8.2.3");var subQ15=sQuery(id+"F0.wireOp",EDGE,"E5");var subQ19=sQuery(id+"F0.wireOp",EDGE,"E8.1.3");var subQ22=sQuery(id+"F0.wireOp",EDGE,"E8.2.0");var subQ24=sQuery(id+"F0.wireOp",EDGE,"E3");var subQ29=sQuery(id+"F0.wireOp",EDGE,"E6");var subQ32=sQuery(id+"F0.wireOp",EDGE,"E8.2.2");var subQ33=sQuery(id+"F0.wireOp",EDGE,"E8.2.1");var subQ43=sQuery(id+"F0.wireOp",EDGE,"E1");var subQ44=sQuery(id+"F0.wireOp",EDGE,"E2");var subQ46=sQuery(id+"F0.wireOp",EDGE,"E14.5.3");var subQ47=sQuery(id+"F0.wireOp",EDGE,"E7");var subQ48=sQuery(id+"F0.wireOp",EDGE,"E14.3.3");var subQ49=sQuery(id+"F0.wireOp",EDGE,"E14.4.1");var subQ50=sQuery(id+"F0.wireOp",EDGE,"E14.5.1");var subQ51=sQuery(id+"F0.wireOp",EDGE,"E14.4.3");var subQ52=sQuery(id+"F0.wireOp",EDGE,"E8.1.1");var subQ53=sQuery(id+"F0.wireOp",EDGE,"E8.1.2");var subQ54=sQuery(id+"F0.wireOp",EDGE,"E14.3.2");var subQ55=sQuery(id+"F0.wireOp",EDGE,"E14.4.2");var subQ56=sQuery(id+"F0.wireOp",EDGE,"E14.5.2");Q1=makeQuery(id+"F2.boolean.opBoolean","SPLIT",FACE,{"disambiguationData":[TD([makeQuery(id+"F1.opExtrude","SWEPT_FACE",FACE,{"disambiguationData":[OSD([subQ43])]})])],"derivedFrom":makeQuery(id+"F1.opExtrude","CAP_FACE",FACE,{"disambiguationData":[OSD([sQuery(id+"F0.wireOp",EDGE,"E0"),subQ43,subQ44,subQ24,subQ15,subQ29,subQ47,subQ11,subQ52,subQ53,subQ19,subQ22,subQ33,subQ32,subQ13,subQ10,subQ9,subQ8,subQ7,subQ6,subQ5,subQ4,subQ3,subQ2,subQ1,subQ0,subQ54,subQ48,subQ49,subQ55,subQ51,subQ50,subQ56,subQ46])],"isStart":true})});}
            chamfer(context, id + "F6", {"entities" : qUnion([Q0, Q1]), "width" : 1.52 * mm, "tangentPropagation" : true});
        }
    });
